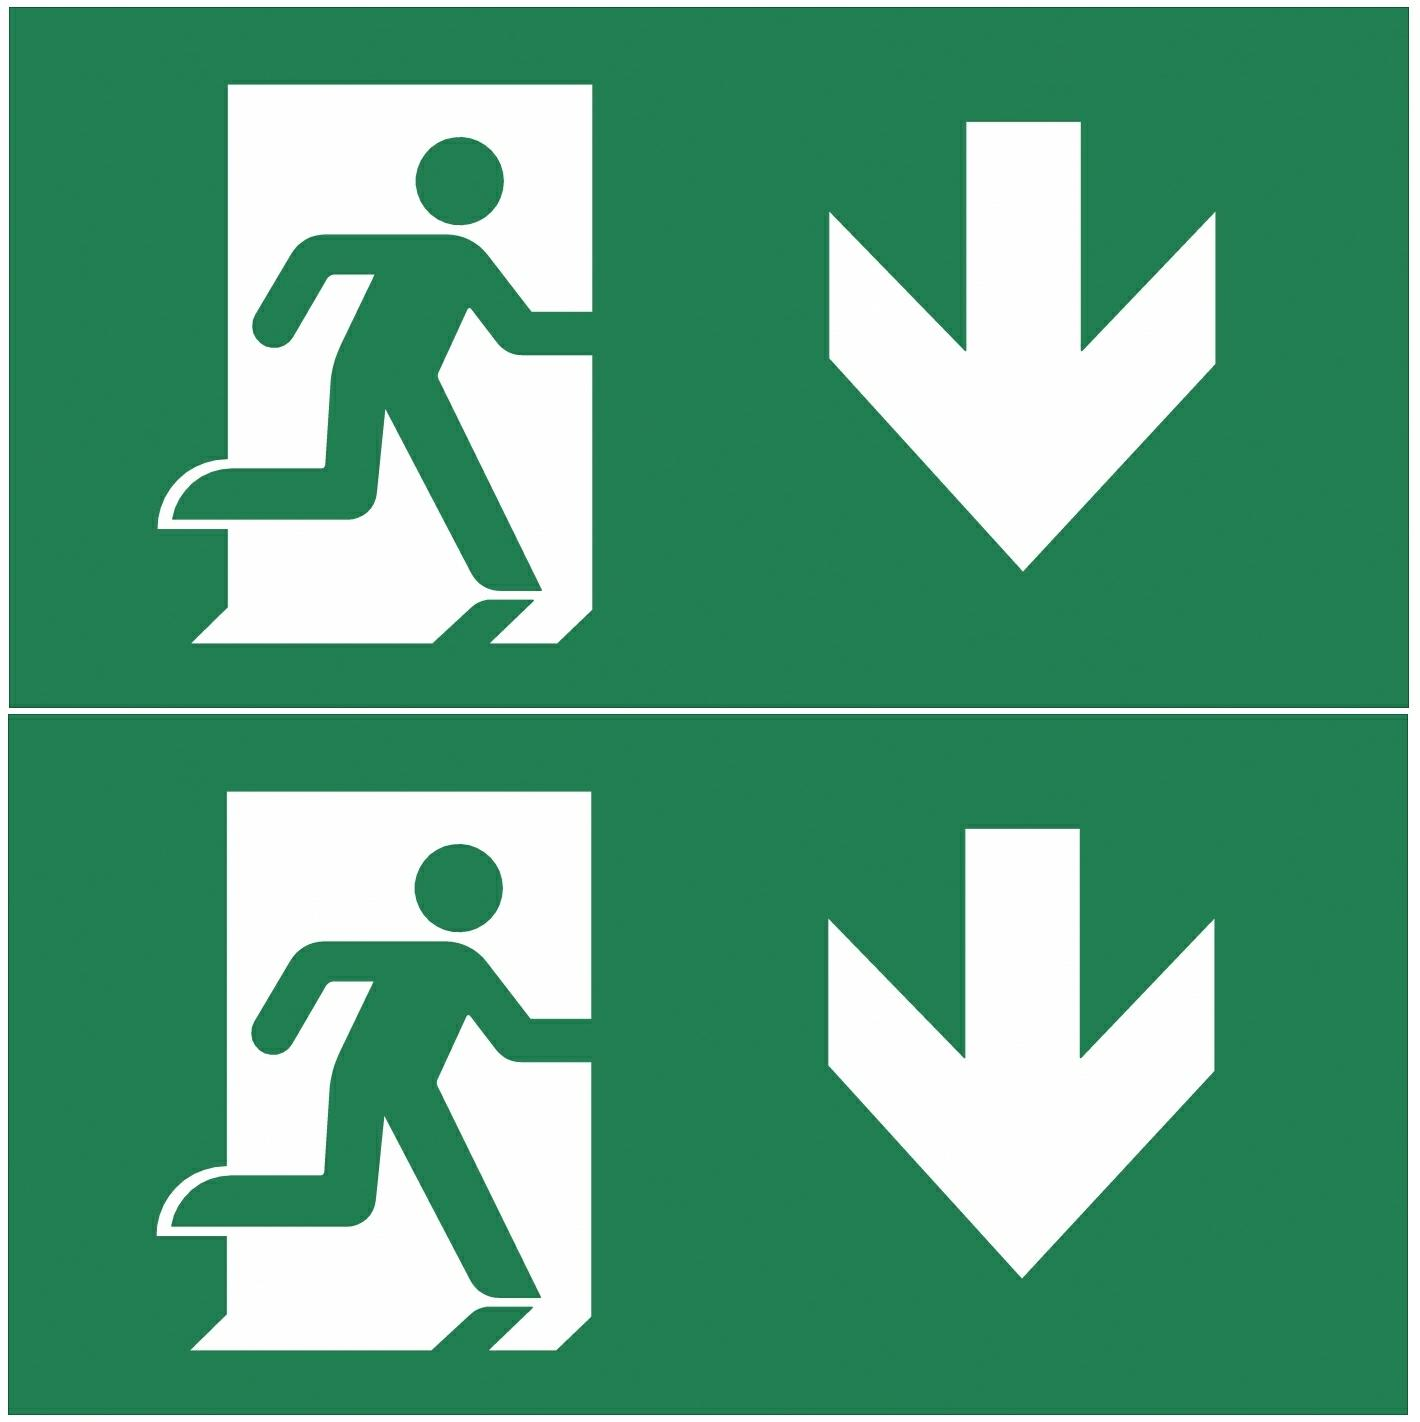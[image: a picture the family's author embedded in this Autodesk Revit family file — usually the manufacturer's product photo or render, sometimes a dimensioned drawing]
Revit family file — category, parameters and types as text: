
# Revit family: TWT8153WA
name_source: partatom
category: Lighting Fixtures
revit_build: Autodesk Revit 2016 (Build: 20150714_1515(x64)
units: mm (PartAtom-declared; Revit-internal decimal feet)

## family parameters
Always vertical = Yes
Cut with Voids When Loaded = No
Light Source = No
OmniClass Number = 23.80.70.00
OmniClass Title = Lighting
Part Type = Normal
Room Calculation Point = No
Round Connector Dimension = Use Diameter
Shared = No
Work Plane-Based = No

## types (4) — shared parameters
Aperture for Recess Mounting = 53 mm x 415 mm
Body Material = Plastic
Color = RAL9003
Customs Code = 94056080
Description = Self-Contained LED Exit Light with 3 h Battery Backup and Wireless Monitoring
ETIM Product Class = EC001957
Electrical Installation = 2/3 x 2,5 mm² -o-
Feature = Aalto Control
GTIN Code = 6438045011929
Glow Wire Test of Plastic Materials = 650 °C
Height = 287 mm
IP Class = IP44
Keynote = 23
Length = 408 mm
Light Source = LED
Manufacturer = Teknoware Oy
Max Input Power VA = 5 VA
Model = ESC 81
Mounting_Optional = Recess, Flag, Pendel
Mounting_Standard = Wall, Ceiling
Nominal Supply Voltage = 220-240 V, 50/60 Hz AC
Product Code = TWT8153WA
Protection Class = II
Sähkönumero = 4281016
Sähkönumerot.fi -tuotesivu = http://www.sahkonumerot.fi
Temperature Range Min_Max = -5...+30 °C
Type Image = ESC81.jpg
URL = http://www.teknoware.com
Viewing Distance = 60000 mm  [stored 196.85 ft]
Weight = 2.10 kg
Width = 40 mm  [stored 0.131234 ft]

## per-type parameters (varying)
| type | Max Input Power W | Pictogram Type |
| Arrow right_left 60m | 3 W | OPASTE PBV81601E |
| Arrow right_left 40m | 3 W | OPASTE PBV81401E |
| Arrow down 60m | 3 W | OPASTE PBV81602E |
| Arrow down 40m | 0 W | OPASTE PBV81402E |

note: [stored X ft] marks values corroborated as IEEE doubles in the binary element streams (Revit-internal decimal feet)

## geometry (parser evidence)
native form markers: Sweep x16
no freeform markers — native parametric forms only
